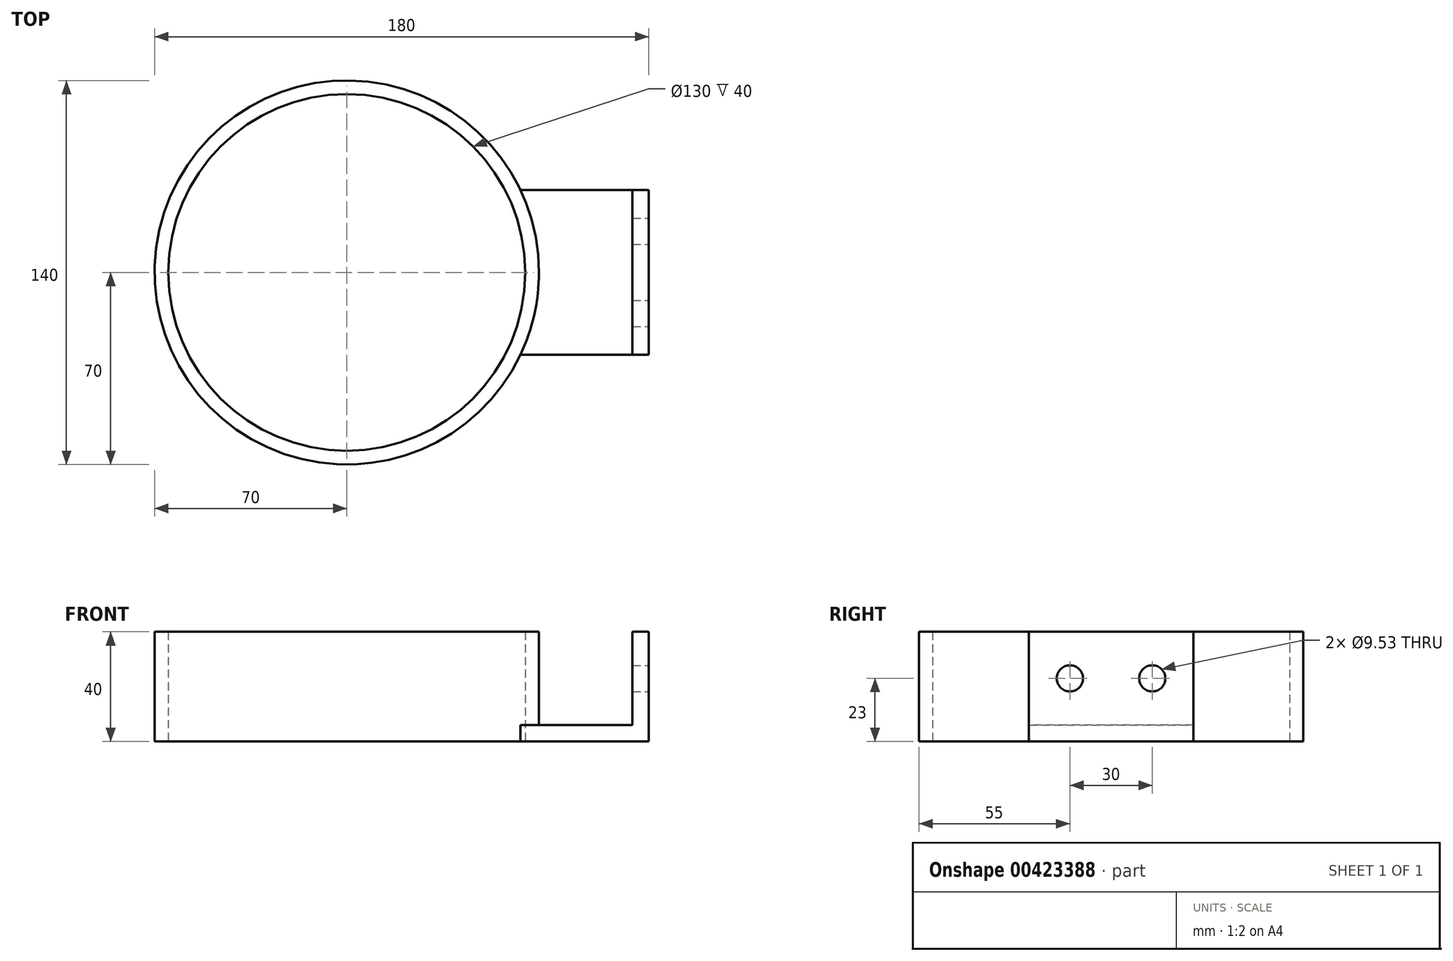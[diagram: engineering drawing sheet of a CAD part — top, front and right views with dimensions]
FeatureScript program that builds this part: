
annotation { "Feature Type Name" : "Feature", "Feature Type Description" : "" }
export const myFeature = defineFeature(function(context is Context, id is Id, definition is map)
    precondition{}
    {
        {
            var Q0;
            Q0=qCreatedBy(makeId("Top.planeOp"),FACE);
            var sketch = newSketch(context, id + "F0", { "sketchPlane" : qUnion([Q0])});
            skCircle(sketch, "E0", {"center": v(0, 0) * mm, "radius": 70 * mm});
            skCircle(sketch, "E1", {"center": v(0, 0) * mm, "radius": 65 * mm});
            skLineSegment(sketch, "E2", {"start": v(110, 0) * mm, "end": v(110, 30) * mm});
            skLineSegment(sketch, "E3", {"start": v(110, 0) * mm, "end": v(110, -30) * mm});
            skLineSegment(sketch, "E4", {"start": v(110, -30) * mm, "end": v(63.25, -30) * mm});
            skLineSegment(sketch, "E5", {"start": v(110, 30) * mm, "end": v(63.25, 30) * mm});
            skLineSegment(sketch, "E6", {"start": v(104, 30) * mm, "end": v(104, -30) * mm});
            skSolve(sketch);
        }
        {
            var Q0;
            Q0=makeQuery(id+"F0.imprint","IMPRINT",FACE,{"disambiguationData":[TD([[makeQuery(id+"F0.imprint","IMPRINT",EDGE,{"derivedFrom":sQuery(id+"F0.wireOp",EDGE,"E1")}),-1.0]])]});
            extrude(context, id + "F1", {"entities" : qUnion([Q0]), "depth" : 40 * mm});
        }
        {
            var Q0;
            {var subQ5=sQuery(id+"F0.wireOp",EDGE,"E6");Q0=makeQuery(id+"F0.imprint","IMPRINT",FACE,{"disambiguationData":[TD([[makeQuery(id+"F0.imprint","IMPRINT",EDGE,{"derivedFrom":subQ5}),-1.0]])]});}
            extrude(context, id + "F2", {"entities" : qUnion([Q0]), "operationType" : NewBodyOperationType.ADD, "depth" : 6 * mm});
        }
        {
            var Q0;
            {var subQ1=sQuery(id+"F0.wireOp",EDGE,"E2");Q0=makeQuery(id+"F0.imprint","IMPRINT",FACE,{"disambiguationData":[TD([[makeQuery(id+"F0.imprint","IMPRINT",EDGE,{"derivedFrom":subQ1}),1.0]])]});}
            extrude(context, id + "F3", {"entities" : qUnion([Q0]), "operationType" : NewBodyOperationType.ADD, "depth" : 40 * mm});
        }
        {
            var Q0;
            Q0=makeQuery(id+"F3.opExtrude","SWEPT_FACE",FACE,{"disambiguationData":[OSD([sQuery(id+"F0.wireOp",EDGE,"E2"),sQuery(id+"F0.wireOp",EDGE,"E3")])]});
            var sketch = newSketch(context, id + "F4", { "sketchPlane" : qUnion([Q0])});
            skCircle(sketch, "E7", {"center": v(-15, 23) * mm, "radius": 4.76 * mm});
            skCircle(sketch, "E8", {"center": v(15, 23) * mm, "radius": 4.76 * mm});
            skSolve(sketch);
        }
        {
            var Q0;
            Q0=makeQuery(id+"F4.imprint","IMPRINT",FACE,{"disambiguationData":[TD([[makeQuery(id+"F4.imprint","IMPRINT",EDGE,{"derivedFrom":sQuery(id+"F4.wireOp",EDGE,"E7")}),1.0]])]});
            var Q1;
            Q1=makeQuery(id+"F4.imprint","IMPRINT",FACE,{"disambiguationData":[TD([[makeQuery(id+"F4.imprint","IMPRINT",EDGE,{"derivedFrom":sQuery(id+"F4.wireOp",EDGE,"E8")}),1.0]])]});
            extrude(context, id + "F5", {"entities" : qUnion([Q0, Q1]), "operationType" : NewBodyOperationType.REMOVE, "oppositeDirection" : true, "depth" : 6 * mm});
        }
    });
